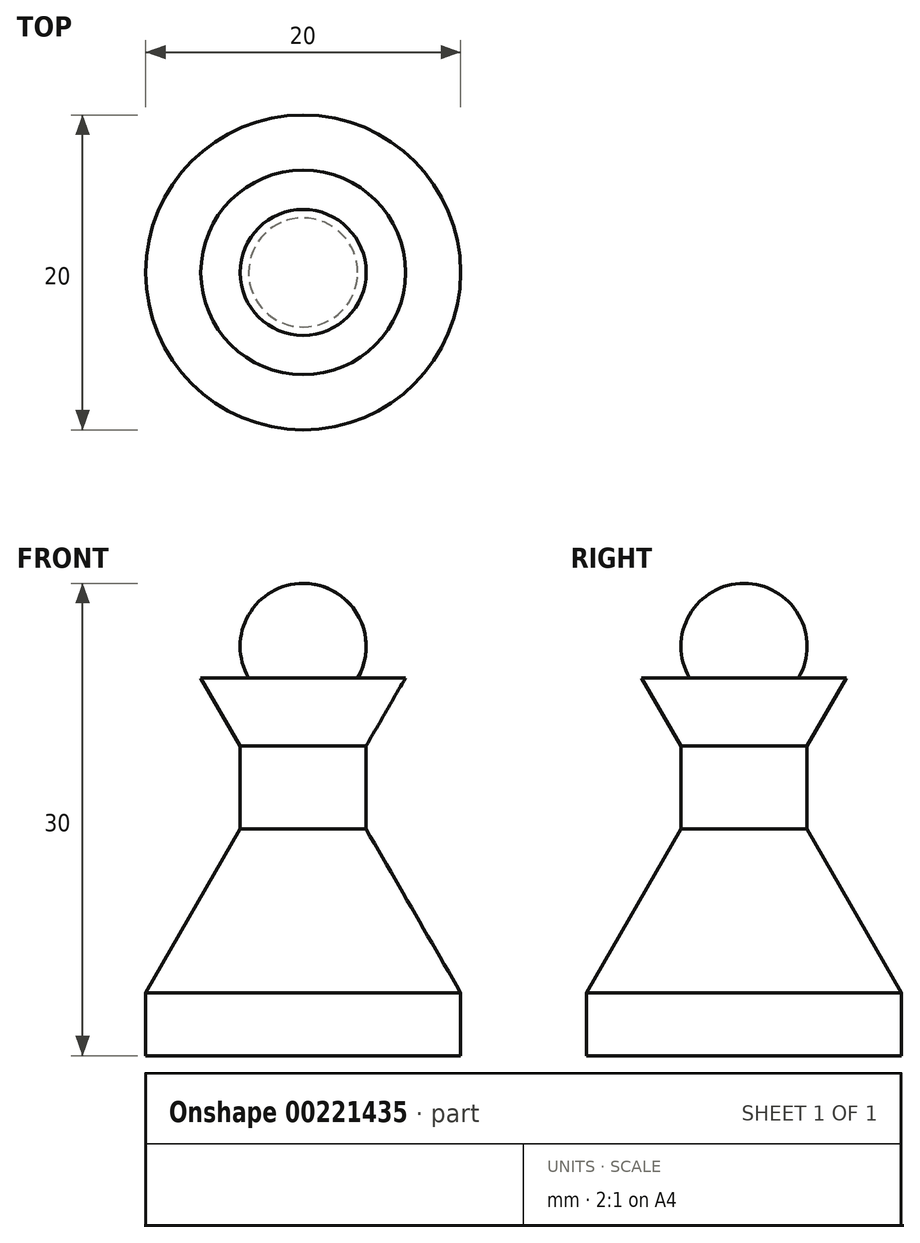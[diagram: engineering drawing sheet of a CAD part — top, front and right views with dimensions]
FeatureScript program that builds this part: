
annotation { "Feature Type Name" : "Feature", "Feature Type Description" : "" }
export const myFeature = defineFeature(function(context is Context, id is Id, definition is map)
    precondition{}
    {
        {
            var Q0;
            Q0=qCreatedBy(makeId("Front.planeOp"),FACE);
            var sketch = newSketch(context, id + "F0", { "sketchPlane" : qUnion([Q0])});
            skLineSegment(sketch, "E0", {"start": v(0, 27.1) * mm, "end": v(0, -8.1) * mm, "construction": true});
            skLineSegment(sketch, "E1", {"start": v(0, 0) * mm, "end": v(10, 0) * mm});
            skLineSegment(sketch, "E2", {"start": v(10, 0) * mm, "end": v(10, 4) * mm});
            skLineSegment(sketch, "E3", {"start": v(4, 14.4) * mm, "end": v(10, 4) * mm});
            skLineSegment(sketch, "E4", {"start": v(4, 14.4) * mm, "end": v(4, 19.67) * mm});
            skLineSegment(sketch, "E5", {"start": v(4, 19.67) * mm, "end": v(6.5, 24) * mm});
            skLineSegment(sketch, "E6", {"start": v(6.5, 24) * mm, "end": v(3.46, 24) * mm});
            skArc(sketch, "E7", {"start": v(3.46, 24) * mm, "mid": v(3.46, 28) * mm, "end": v(0, 30) * mm});
            skLineSegment(sketch, "E8", {"start": v(0, 30) * mm, "end": v(0, 0) * mm});
            skSolve(sketch);
        }
        {
            var Q0;
            Q0 = qSketchRegion(id + "F0", true);
            var Q1;
            Q1=sQuery(id+"F0.wireOp",EDGE,"E0");
            revolve(context, id + "F1", {"entities" : qUnion([Q0]), "axis" : qUnion([Q1]), "revolveType" : RevolveType.FULL});
        }
    });
